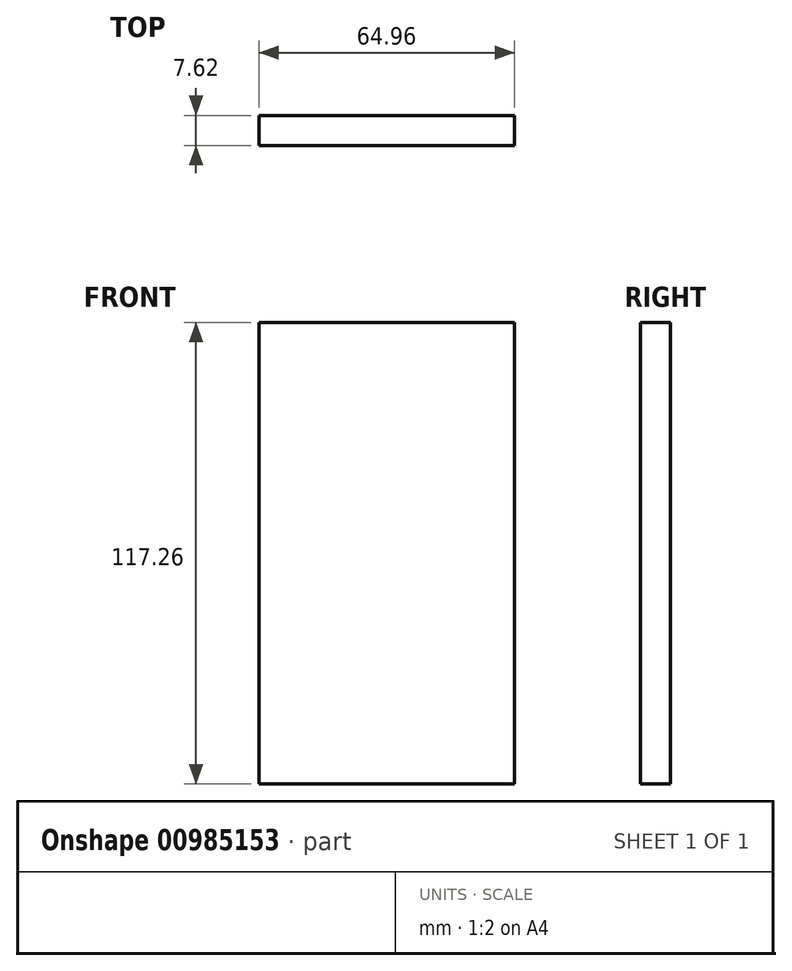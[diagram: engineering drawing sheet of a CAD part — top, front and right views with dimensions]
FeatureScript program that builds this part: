
annotation { "Feature Type Name" : "Feature", "Feature Type Description" : "" }
export const myFeature = defineFeature(function(context is Context, id is Id, definition is map)
    precondition{}
    {
        {
            var Q0;
            Q0=qCreatedBy(makeId("Front.planeOp"),FACE);
            var sketch = newSketch(context, id + "F0", { "sketchPlane" : qUnion([Q0])});
            skLineSegment(sketch, "E0.bottom", {"start": v(-60.14, 58.5) * mm, "end": v(4.82, 58.5) * mm});
            skLineSegment(sketch, "E0.top", {"start": v(-60.14, -58.75) * mm, "end": v(4.82, -58.75) * mm});
            skLineSegment(sketch, "E0.left", {"start": v(-60.14, 58.5) * mm, "end": v(-60.14, -58.75) * mm});
            skLineSegment(sketch, "E0.right", {"start": v(4.82, 58.5) * mm, "end": v(4.82, -58.75) * mm});
            skSolve(sketch);
        }
        {
            var Q0;
            Q0=makeQuery(id+"F0.imprint","IMPRINT",FACE,{"disambiguationData":[TD([[makeQuery(id+"F0.imprint","IMPRINT",EDGE,{"derivedFrom":sQuery(id+"F0.wireOp",EDGE,"E0.bottom")}),-1.0]])]});
            extrude(context, id + "F1", {"entities" : qUnion([Q0]), "depth" : 7.62 * mm, "offsetDistance" : 25.4 * mm});
        }
    });
